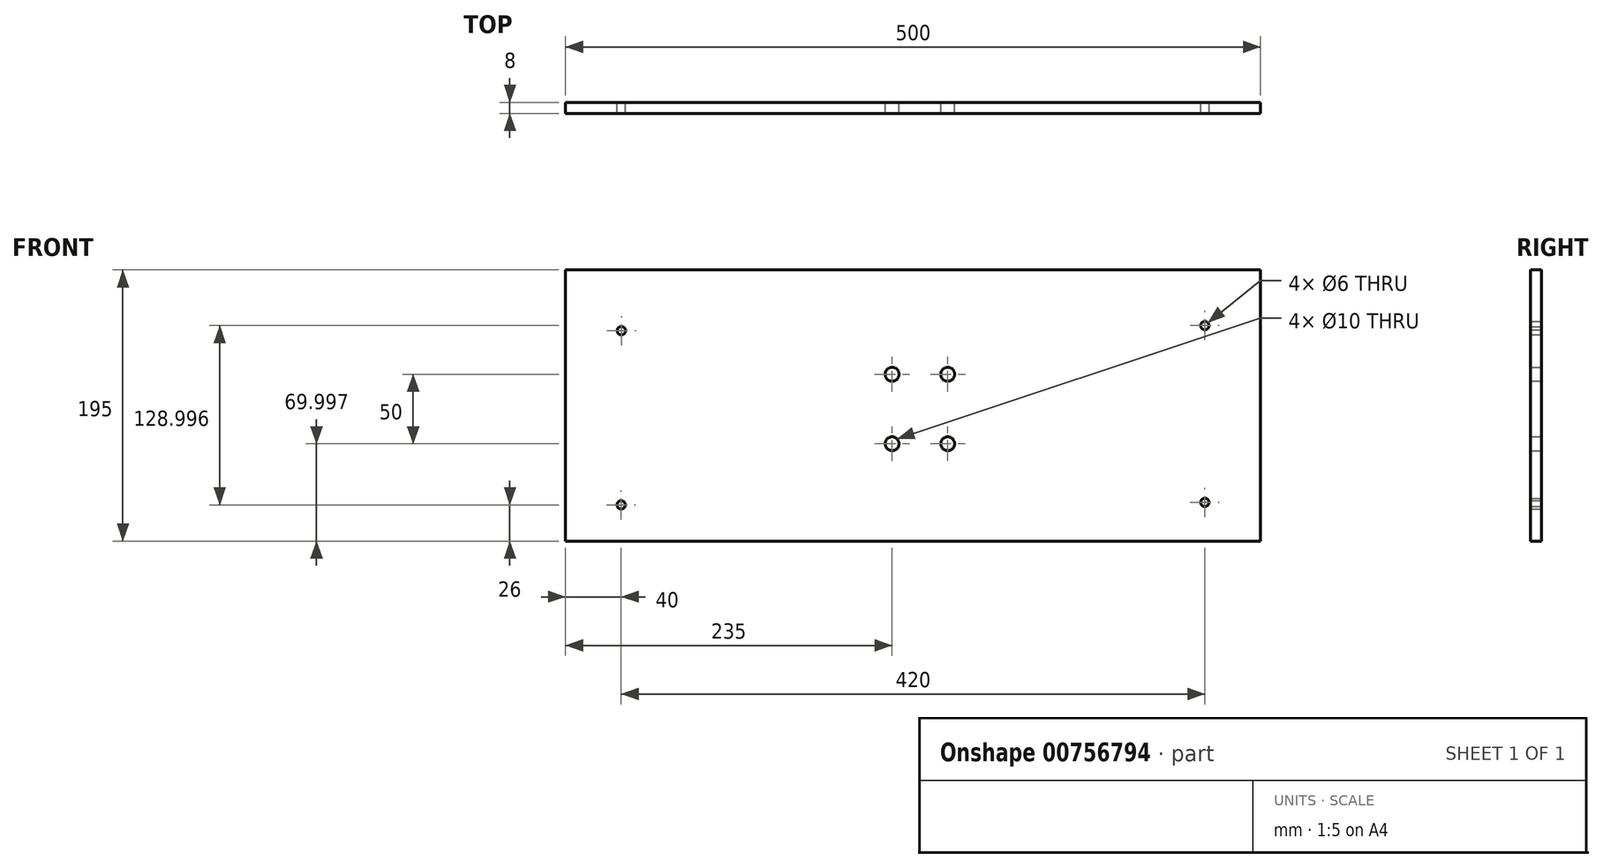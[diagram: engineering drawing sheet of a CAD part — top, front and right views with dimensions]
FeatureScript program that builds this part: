
annotation { "Feature Type Name" : "Feature", "Feature Type Description" : "" }
export const myFeature = defineFeature(function(context is Context, id is Id, definition is map)
    precondition{}
    {
        {
            var Q0;
            Q0=qCreatedBy(makeId("Front.planeOp"),FACE);
            var sketch = newSketch(context, id + "F0", { "sketchPlane" : qUnion([Q0])});
            skLineSegment(sketch, "E0.bottom", {"start": v(-73.73, 167.2) * mm, "end": v(426.27, 167.2) * mm});
            skLineSegment(sketch, "E0.top", {"start": v(-73.73, -27.8) * mm, "end": v(426.27, -27.8) * mm});
            skLineSegment(sketch, "E0.left", {"start": v(-73.73, 167.2) * mm, "end": v(-73.73, -27.8) * mm});
            skLineSegment(sketch, "E0.right", {"start": v(426.27, 167.2) * mm, "end": v(426.27, -27.8) * mm});
            skCircle(sketch, "E1", {"center": v(-33.73, -1.8) * mm, "radius": 3 * mm});
            skCircle(sketch, "E2", {"center": v(-33.56, 123.5) * mm, "radius": 3 * mm});
            skCircle(sketch, "E3", {"center": v(386.27, 127.2) * mm, "radius": 3 * mm});
            skCircle(sketch, "E4", {"center": v(386.27, 0) * mm, "radius": 3 * mm});
            skCircle(sketch, "E5", {"center": v(161.27, 92.2) * mm, "radius": 5 * mm});
            skCircle(sketch, "E6", {"center": v(201.27, 92.2) * mm, "radius": 5 * mm});
            skCircle(sketch, "E7", {"center": v(201.27, 42.2) * mm, "radius": 5 * mm});
            skCircle(sketch, "E8", {"center": v(161.27, 42.2) * mm, "radius": 5 * mm});
            skSolve(sketch);
        }
        {
            var Q0;
            Q0=makeQuery(id+"F0.imprint","IMPRINT",FACE,{"disambiguationData":[TD([[makeQuery(id+"F0.imprint","IMPRINT",EDGE,{"derivedFrom":sQuery(id+"F0.wireOp",EDGE,"E0.bottom")}),-1.0]])]});
            extrude(context, id + "F1", {"entities" : qUnion([Q0]), "depth" : 8 * mm, "offsetDistance" : 25 * mm});
        }
    });
